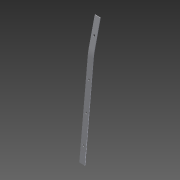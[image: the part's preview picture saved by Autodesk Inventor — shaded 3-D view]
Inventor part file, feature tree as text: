
AUTODESK INVENTOR PART (.ipt)
format: ipt  version: 2015 (Build 190159000, 159)  size: 132,608 bytes
history: native  units: mm
features: reference x11, sketch x6, other x3, hole x3, sweep x1
ambient origin geometry x8: Origin, YZ Plane, XZ Plane, XY Plane, X Axis, Y Axis, Z Axis, Center Point
bodies: Body1 (feature_tree)
feature tree (24):
  other  "Listwa_siedziska_lewa"
  sweep  "Przeciągnięcie1"
  hole  "Otwór1"  [1 undecoded]
  other  "Gięcie części1"
  hole  "Otwór3"  [1 undecoded]
  hole  "Otwór4"  [1 undecoded]
  sketch  "Szkic1"
  sketch  "Szkic2"
  sketch  "Szkic4"
  reference  "Odniesienie1"
  reference  "Odniesienie2"
  reference  "Odniesienie3"
  reference  "Odniesienie4"
  sketch  "Szkic5"
  sketch  "Szkic6"
  other  "Bryła2"
  reference  "Odniesienie6"
  reference  "Odniesienie7"
  reference  "Odniesienie8"
  reference  "Odniesienie9"
  reference  "Odniesienie10"
  reference  "Odniesienie11"
  sketch  "Szkic7"
  reference  "Odniesienie12"
note: 3 required parameter values undecoded (feature->parameter linkage not recoverable at this tier; creation-order binding heuristic only, values carry confidence <= 0.55)
